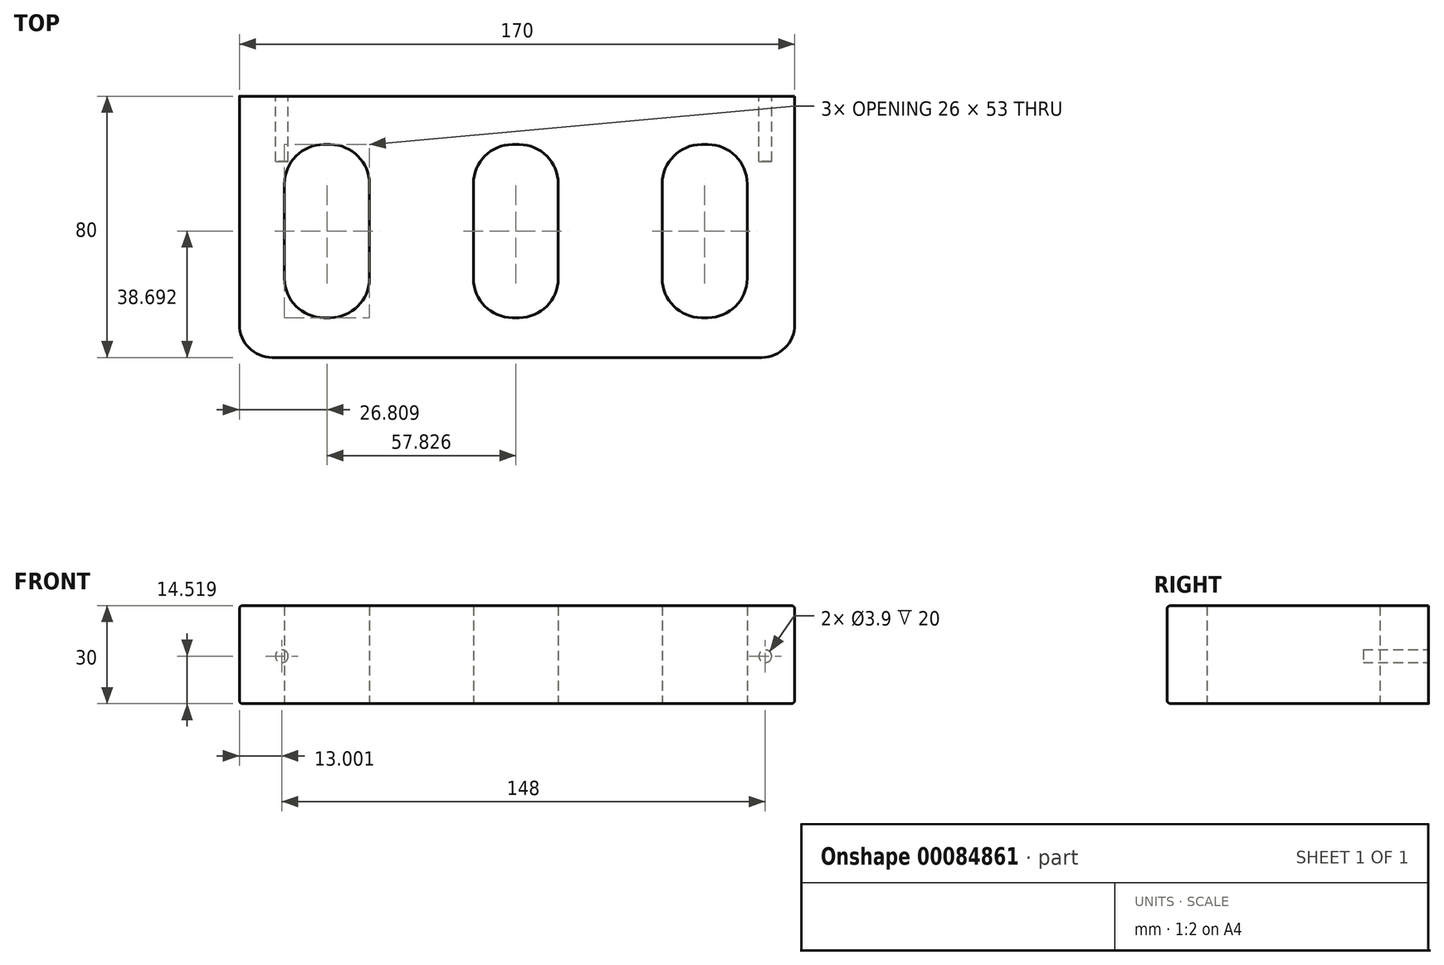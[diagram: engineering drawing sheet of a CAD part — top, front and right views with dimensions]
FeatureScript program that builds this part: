
annotation { "Feature Type Name" : "Feature", "Feature Type Description" : "" }
export const myFeature = defineFeature(function(context is Context, id is Id, definition is map)
    precondition{}
    {
        {
            var Q0;
            Q0=qCreatedBy(makeId("Top.planeOp"),FACE);
            var sketch = newSketch(context, id + "F0", { "sketchPlane" : qUnion([Q0])});
            skLineSegment(sketch, "E0.bottom", {"start": v(-90.25, 33.75) * mm, "end": v(79.75, 33.75) * mm});
            skLineSegment(sketch, "E0.top", {"start": v(-90.25, -46.25) * mm, "end": v(79.75, -46.25) * mm});
            skLineSegment(sketch, "E0.left", {"start": v(-90.25, 33.75) * mm, "end": v(-90.25, -46.25) * mm});
            skLineSegment(sketch, "E0.right", {"start": v(79.75, 33.75) * mm, "end": v(79.75, -46.25) * mm});
            skLineSegment(sketch, "E1.bottom", {"start": v(-76.44, 18.94) * mm, "end": v(-50.44, 18.94) * mm});
            skLineSegment(sketch, "E1.top", {"start": v(-76.44, -34.06) * mm, "end": v(-50.44, -34.06) * mm});
            skLineSegment(sketch, "E1.left", {"start": v(-76.44, 18.94) * mm, "end": v(-76.44, -34.06) * mm});
            skLineSegment(sketch, "E1.right", {"start": v(-50.44, 18.94) * mm, "end": v(-50.44, -34.06) * mm});
            skLineSegment(sketch, "E2.1.0.0", {"start": v(-18.61, 18.94) * mm, "end": v(-18.61, -34.06) * mm});
            skLineSegment(sketch, "E2.1.0.1", {"start": v(-18.61, 18.94) * mm, "end": v(7.39, 18.94) * mm});
            skLineSegment(sketch, "E2.1.0.2", {"start": v(7.39, 18.94) * mm, "end": v(7.39, -34.06) * mm});
            skLineSegment(sketch, "E2.1.0.3", {"start": v(-18.61, -34.06) * mm, "end": v(7.39, -34.06) * mm});
            skLineSegment(sketch, "E2.2.0.0", {"start": v(39.21, 18.94) * mm, "end": v(39.21, -34.06) * mm});
            skLineSegment(sketch, "E2.2.0.1", {"start": v(39.21, 18.94) * mm, "end": v(65.21, 18.94) * mm});
            skLineSegment(sketch, "E2.2.0.2", {"start": v(65.21, 18.94) * mm, "end": v(65.21, -34.06) * mm});
            skLineSegment(sketch, "E2.2.0.3", {"start": v(39.21, -34.06) * mm, "end": v(65.21, -34.06) * mm});
            skLineSegment(sketch, "E2.direction1", {"start": v(-76.44, -34.06) * mm, "end": v(-18.61, -34.06) * mm, "construction": true});
            skSolve(sketch);
        }
        {
            var Q0;
            Q0=makeQuery(id+"F0.imprint","IMPRINT",FACE,{"disambiguationData":[TD([[makeQuery(id+"F0.imprint","IMPRINT",EDGE,{"derivedFrom":sQuery(id+"F0.wireOp",EDGE,"E0.bottom")}),-1.0]])]});
            extrude(context, id + "F1", {"entities" : qUnion([Q0]), "depth" : 30 * mm});
        }
        {
            var Q0;
            Q0=makeQuery(id+"F1.opExtrude","SWEPT_EDGE",EDGE,{"disambiguationData":[OSD([sQuery(id+"F0.wireOp",EDGE,"E0.top"),sQuery(id+"F0.wireOp",EDGE,"E0.left")])]});
            var Q1;
            Q1=makeQuery(id+"F1.opExtrude","SWEPT_EDGE",EDGE,{"disambiguationData":[OSD([sQuery(id+"F0.wireOp",EDGE,"E0.top"),sQuery(id+"F0.wireOp",EDGE,"E0.right")])]});
            fillet(context, id + "F2", {"entities" : qUnion([Q0, Q1]), "radius" : 10.05 * mm, "tangentPropagation" : true, "allowEdgeOverflow" : false});
        }
        {
            var Q0;
            Q0=makeQuery(id+"F1.opExtrude","SWEPT_EDGE",EDGE,{"disambiguationData":[OSD([sQuery(id+"F0.wireOp",EDGE,"E1.bottom"),sQuery(id+"F0.wireOp",EDGE,"E1.right")])]});
            var Q1;
            Q1=makeQuery(id+"F1.opExtrude","SWEPT_EDGE",EDGE,{"disambiguationData":[OSD([sQuery(id+"F0.wireOp",EDGE,"E2.1.0.1"),sQuery(id+"F0.wireOp",EDGE,"E2.1.0.2")])]});
            var Q2;
            Q2=makeQuery(id+"F1.opExtrude","SWEPT_EDGE",EDGE,{"disambiguationData":[OSD([sQuery(id+"F0.wireOp",EDGE,"E2.2.0.1"),sQuery(id+"F0.wireOp",EDGE,"E2.2.0.2")])]});
            var Q3;
            Q3=makeQuery(id+"F1.opExtrude","SWEPT_EDGE",EDGE,{"disambiguationData":[OSD([sQuery(id+"F0.wireOp",EDGE,"E1.bottom"),sQuery(id+"F0.wireOp",EDGE,"E1.left")])]});
            var Q4;
            Q4=makeQuery(id+"F1.opExtrude","SWEPT_EDGE",EDGE,{"disambiguationData":[OSD([sQuery(id+"F0.wireOp",EDGE,"E2.1.0.0"),sQuery(id+"F0.wireOp",EDGE,"E2.1.0.1")])]});
            var Q5;
            Q5=makeQuery(id+"F1.opExtrude","SWEPT_EDGE",EDGE,{"disambiguationData":[OSD([sQuery(id+"F0.wireOp",EDGE,"E2.2.0.0"),sQuery(id+"F0.wireOp",EDGE,"E2.2.0.1")])]});
            var Q6;
            Q6=makeQuery(id+"F1.opExtrude","SWEPT_EDGE",EDGE,{"disambiguationData":[OSD([sQuery(id+"F0.wireOp",EDGE,"E2.2.0.0"),sQuery(id+"F0.wireOp",EDGE,"E2.2.0.3")])]});
            var Q7;
            Q7=makeQuery(id+"F1.opExtrude","SWEPT_EDGE",EDGE,{"disambiguationData":[OSD([sQuery(id+"F0.wireOp",EDGE,"E2.1.0.0"),sQuery(id+"F0.wireOp",EDGE,"E2.1.0.3")])]});
            var Q8;
            Q8=makeQuery(id+"F1.opExtrude","SWEPT_EDGE",EDGE,{"disambiguationData":[OSD([sQuery(id+"F0.wireOp",EDGE,"E1.top"),sQuery(id+"F0.wireOp",EDGE,"E1.left")])]});
            var Q9;
            Q9=makeQuery(id+"F1.opExtrude","SWEPT_EDGE",EDGE,{"disambiguationData":[OSD([sQuery(id+"F0.wireOp",EDGE,"E1.top"),sQuery(id+"F0.wireOp",EDGE,"E1.right")])]});
            var Q10;
            Q10=makeQuery(id+"F1.opExtrude","SWEPT_EDGE",EDGE,{"disambiguationData":[OSD([sQuery(id+"F0.wireOp",EDGE,"E2.1.0.2"),sQuery(id+"F0.wireOp",EDGE,"E2.1.0.3")])]});
            var Q11;
            Q11=makeQuery(id+"F1.opExtrude","SWEPT_EDGE",EDGE,{"disambiguationData":[OSD([sQuery(id+"F0.wireOp",EDGE,"E2.2.0.2"),sQuery(id+"F0.wireOp",EDGE,"E2.2.0.3")])]});
            fillet(context, id + "F3", {"entities" : qUnion([Q0, Q1, Q2, Q3, Q4, Q5, Q6, Q7, Q8, Q9, Q10, Q11]), "radius" : 12 * mm, "tangentPropagation" : true, "allowEdgeOverflow" : false});
        }
        {
            var Q0;
            Q0=makeQuery(id+"F1.opExtrude","CAP_EDGE",EDGE,{"disambiguationData":[OSD([sQuery(id+"F0.wireOp",EDGE,"E0.left")])],"isStart":false});
            var Q1;
            {var subQ0=sQuery(id+"F0.wireOp",EDGE,"E0.left");var subQ1=sQuery(id+"F0.wireOp",EDGE,"E0.top");Q1=makeQuery(id+"F2.opFillet","BLEND_EDGE",EDGE,{"blendedFrom":[makeQuery(id+"F1.opExtrude","SWEPT_EDGE",EDGE,{"disambiguationData":[OSD([subQ1,subQ0])]}),makeQuery(id+"F1.opExtrude","CAP_FACE",FACE,{"disambiguationData":[OSD([sQuery(id+"F0.wireOp",EDGE,"E0.bottom"),subQ1,subQ0,sQuery(id+"F0.wireOp",EDGE,"E0.right"),sQuery(id+"F0.wireOp",EDGE,"E1.bottom"),sQuery(id+"F0.wireOp",EDGE,"E1.top"),sQuery(id+"F0.wireOp",EDGE,"E1.left"),sQuery(id+"F0.wireOp",EDGE,"E1.right"),sQuery(id+"F0.wireOp",EDGE,"E2.1.0.0"),sQuery(id+"F0.wireOp",EDGE,"E2.1.0.1"),sQuery(id+"F0.wireOp",EDGE,"E2.1.0.2"),sQuery(id+"F0.wireOp",EDGE,"E2.1.0.3"),sQuery(id+"F0.wireOp",EDGE,"E2.2.0.0"),sQuery(id+"F0.wireOp",EDGE,"E2.2.0.1"),sQuery(id+"F0.wireOp",EDGE,"E2.2.0.2"),sQuery(id+"F0.wireOp",EDGE,"E2.2.0.3")])],"isStart":false})],"blendedInto":[makeQuery(id+"F1.opExtrude","CAP_FACE",FACE,{"disambiguationData":[OSD([sQuery(id+"F0.wireOp",EDGE,"E0.bottom"),subQ1,subQ0,sQuery(id+"F0.wireOp",EDGE,"E0.right"),sQuery(id+"F0.wireOp",EDGE,"E1.bottom"),sQuery(id+"F0.wireOp",EDGE,"E1.top"),sQuery(id+"F0.wireOp",EDGE,"E1.left"),sQuery(id+"F0.wireOp",EDGE,"E1.right"),sQuery(id+"F0.wireOp",EDGE,"E2.1.0.0"),sQuery(id+"F0.wireOp",EDGE,"E2.1.0.1"),sQuery(id+"F0.wireOp",EDGE,"E2.1.0.2"),sQuery(id+"F0.wireOp",EDGE,"E2.1.0.3"),sQuery(id+"F0.wireOp",EDGE,"E2.2.0.0"),sQuery(id+"F0.wireOp",EDGE,"E2.2.0.1"),sQuery(id+"F0.wireOp",EDGE,"E2.2.0.2"),sQuery(id+"F0.wireOp",EDGE,"E2.2.0.3")])],"isStart":false})]});}
            var Q2;
            Q2=makeQuery(id+"F1.opExtrude","CAP_EDGE",EDGE,{"disambiguationData":[OSD([sQuery(id+"F0.wireOp",EDGE,"E0.right")])],"isStart":true});
            fillet(context, id + "F4", {"entities" : qUnion([Q0, Q1, Q2]), "radius" : 1 * mm, "tangentPropagation" : true, "allowEdgeOverflow" : false});
        }
        {
            var Q0;
            Q0=makeQuery(id+"F1.opExtrude","SWEPT_FACE",FACE,{"disambiguationData":[OSD([sQuery(id+"F0.wireOp",EDGE,"E0.bottom")])]});
            var sketch = newSketch(context, id + "F5", { "sketchPlane" : qUnion([Q0])});
            skCircle(sketch, "E3", {"center": v(-70.75, 14.52) * mm, "radius": 1.95 * mm});
            skCircle(sketch, "E4.1.0.0", {"center": v(77.25, 14.52) * mm, "radius": 1.95 * mm});
            skLineSegment(sketch, "E4.direction1", {"start": v(-70.75, 14.52) * mm, "end": v(77.25, 14.52) * mm, "construction": true});
            skSolve(sketch);
        }
        {
            var Q0;
            Q0=makeQuery(id+"F5.imprint","IMPRINT",FACE,{"disambiguationData":[TD([[makeQuery(id+"F5.imprint","IMPRINT",EDGE,{"derivedFrom":sQuery(id+"F5.wireOp",EDGE,"E3")}),1.0]])]});
            var Q1;
            Q1=makeQuery(id+"F5.imprint","IMPRINT",FACE,{"disambiguationData":[TD([[makeQuery(id+"F5.imprint","IMPRINT",EDGE,{"derivedFrom":sQuery(id+"F5.wireOp",EDGE,"E4.1.0.0")}),1.0]])]});
            var Q2;
            Q2=sQuery(id+"F5.wireOp",EDGE,"E3");
            var Q3;
            Q3=sQuery(id+"F5.wireOp",EDGE,"E4.1.0.0");
            extrude(context, id + "F6", {"entities" : qUnion([Q0, Q1]), "operationType" : NewBodyOperationType.REMOVE, "surfaceEntities" : qUnion([Q2, Q3]), "oppositeDirection" : true, "depth" : 20 * mm});
        }
    });
